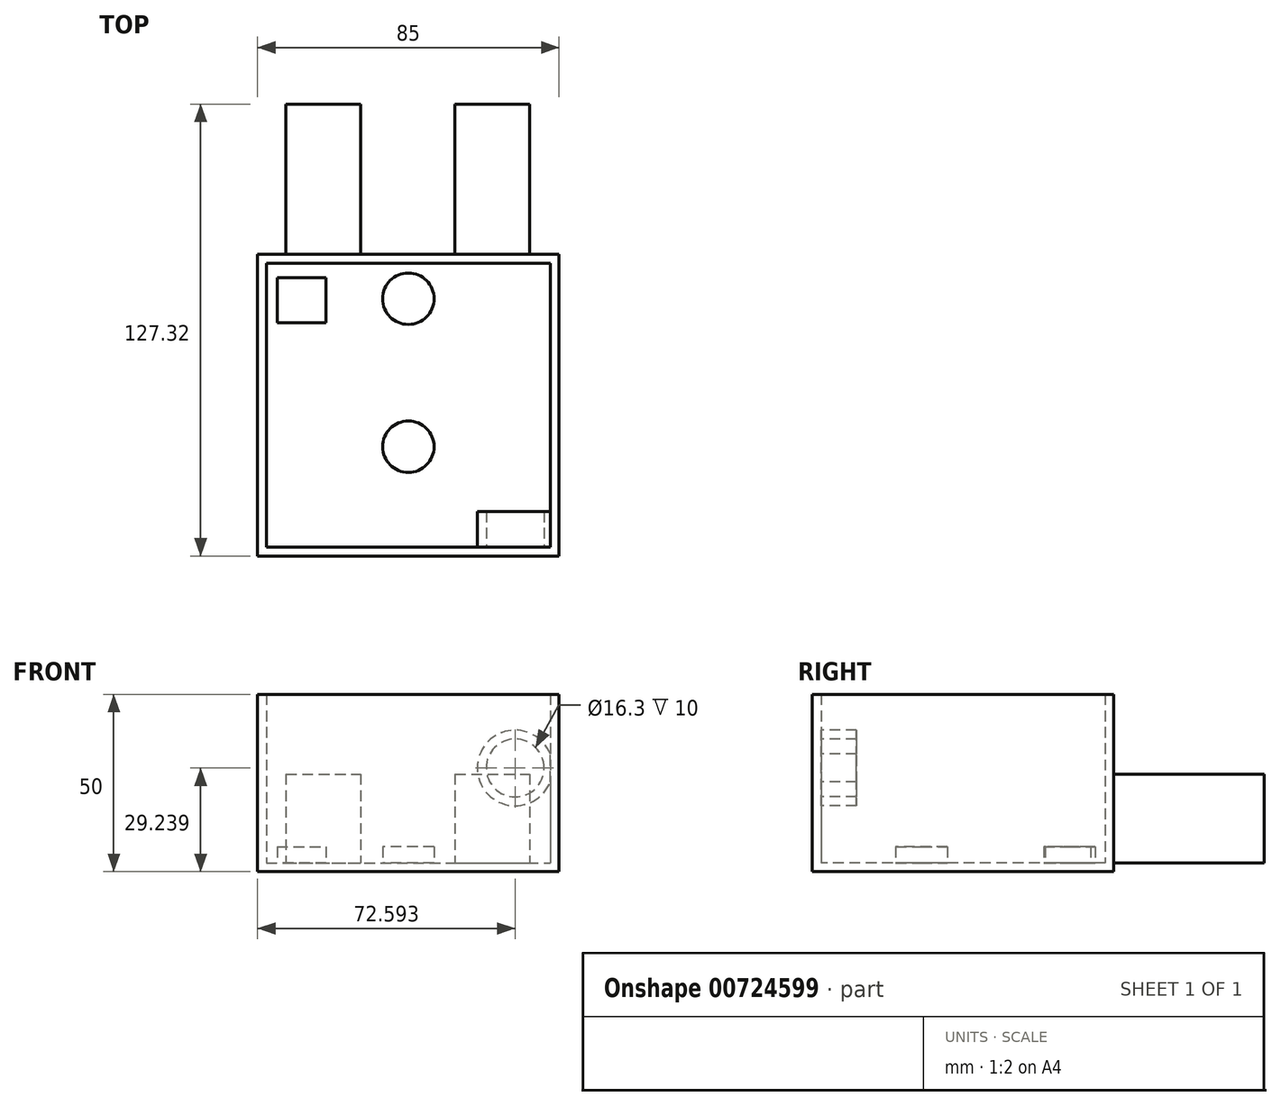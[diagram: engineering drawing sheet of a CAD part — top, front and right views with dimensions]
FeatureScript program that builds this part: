
annotation { "Feature Type Name" : "Feature", "Feature Type Description" : "" }
export const myFeature = defineFeature(function(context is Context, id is Id, definition is map)
    precondition{}
    {
        {
            var Q0;
            Q0=qCreatedBy(makeId("Top.planeOp"),FACE);
            var sketch = newSketch(context, id + "F0", { "sketchPlane" : qUnion([Q0])});
            skLineSegment(sketch, "E0.bottom", {"start": v(-42.5, 42.5) * mm, "end": v(42.5, 42.5) * mm});
            skLineSegment(sketch, "E0.top", {"start": v(-42.5, -42.5) * mm, "end": v(42.5, -42.5) * mm});
            skLineSegment(sketch, "E0.left", {"start": v(-42.5, 42.5) * mm, "end": v(-42.5, -42.5) * mm});
            skLineSegment(sketch, "E0.right", {"start": v(42.5, 42.5) * mm, "end": v(42.5, -42.5) * mm});
            skPoint(sketch, "E0.middle", {"position": v(0, 0) * mm});
            skSolve(sketch);
        }
        {
            var Q0;
            Q0=makeQuery(id+"F0.imprint","IMPRINT",FACE,{"disambiguationData":[TD([[makeQuery(id+"F0.imprint","IMPRINT",EDGE,{"derivedFrom":sQuery(id+"F0.wireOp",EDGE,"E0.bottom")}),-1.0]])]});
            extrude(context, id + "F1", {"entities" : qUnion([Q0]), "depth" : 50 * mm, "offsetDistance" : 25 * mm});
        }
        {
            var Q0;
            Q0=makeQuery(id+"F1.opExtrude","CAP_FACE",FACE,{"disambiguationData":[OSD([sQuery(id+"F0.wireOp",EDGE,"E0.bottom"),sQuery(id+"F0.wireOp",EDGE,"E0.top"),sQuery(id+"F0.wireOp",EDGE,"E0.left"),sQuery(id+"F0.wireOp",EDGE,"E0.right")])],"isStart":false});
            shell(context, id + "F2", {"entities" : qUnion([Q0]), "thickness" : 2.5 * mm});
        }
        {
            var Q0;
            Q0=makeQuery(id+"F2.opShell","OFFSET_FACE",FACE,{"disambiguationData":[OSD([sQuery(id+"F0.wireOp",EDGE,"E0.bottom"),sQuery(id+"F0.wireOp",EDGE,"E0.top"),sQuery(id+"F0.wireOp",EDGE,"E0.left"),sQuery(id+"F0.wireOp",EDGE,"E0.right")])]});
            var sketch = newSketch(context, id + "F3", { "sketchPlane" : qUnion([Q0])});
            skLineSegment(sketch, "E1.bottom", {"start": v(-13.46, 84.82) * mm, "end": v(-34.46, 84.82) * mm});
            skLineSegment(sketch, "E1.top", {"start": v(-13.46, 42.42) * mm, "end": v(-34.46, 42.42) * mm});
            skLineSegment(sketch, "E1.left", {"start": v(-13.46, 84.82) * mm, "end": v(-13.46, 42.42) * mm});
            skLineSegment(sketch, "E1.right", {"start": v(-34.46, 84.82) * mm, "end": v(-34.46, 42.42) * mm});
            skPoint(sketch, "E1.middle", {"position": v(-23.96, 63.62) * mm});
            skLineSegment(sketch, "E2.bottom", {"start": v(13.16, 84.82) * mm, "end": v(34.16, 84.82) * mm});
            skLineSegment(sketch, "E2.top", {"start": v(13.16, 42.42) * mm, "end": v(34.16, 42.42) * mm});
            skLineSegment(sketch, "E2.left", {"start": v(13.16, 84.82) * mm, "end": v(13.16, 42.42) * mm});
            skLineSegment(sketch, "E2.right", {"start": v(34.16, 84.82) * mm, "end": v(34.16, 42.42) * mm});
            skPoint(sketch, "E2.middle", {"position": v(23.66, 63.62) * mm});
            skSolve(sketch);
        }
        {
            var Q0;
            Q0=qSketchRegion(id+"F3",true);
            extrude(context, id + "F4", {"entities" : qUnion([Q0]), "operationType" : NewBodyOperationType.ADD, "depth" : 25 * mm, "offsetDistance" : 25 * mm});
        }
        {
            var Q0;
            Q0=makeQuery(id+"F2.opShell","OFFSET_FACE",FACE,{"disambiguationData":[OSD([sQuery(id+"F0.wireOp",EDGE,"E0.bottom"),sQuery(id+"F0.wireOp",EDGE,"E0.top"),sQuery(id+"F0.wireOp",EDGE,"E0.left"),sQuery(id+"F0.wireOp",EDGE,"E0.right")])]});
            var sketch = newSketch(context, id + "F5", { "sketchPlane" : qUnion([Q0])});
            skLineSegment(sketch, "E3", {"start": v(-40, -21.26) * mm, "end": v(40, -21.26) * mm});
            skLineSegment(sketch, "E4", {"start": v(-40, 0) * mm, "end": v(40, 0) * mm});
            skLineSegment(sketch, "E5", {"start": v(-40, 21.59) * mm, "end": v(40, 21.59) * mm});
            skSolve(sketch);
        }
        {
            var Q0;
            Q0=sQuery(id+"F5.wireOp",EDGE,"E5");
            var Q1;
            Q1=sQuery(id+"F5.wireOp",EDGE,"E4");
            var Q2;
            Q2=sQuery(id+"F5.wireOp",EDGE,"E3");
            extrude(context, id + "F6", {"bodyType" : ToolBodyType.SURFACE, "surfaceEntities" : qUnion([Q0, Q1, Q2]), "depth" : 30 * mm, "offsetDistance" : 25 * mm});
        }
        {
            var Q0;
            Q0=makeQuery(id+"F2.opShell","OFFSET_FACE",FACE,{"disambiguationData":[OSD([sQuery(id+"F0.wireOp",EDGE,"E0.top")])]});
            var sketch = newSketch(context, id + "F7", { "sketchPlane" : qUnion([Q0])});
            skCircle(sketch, "E6", {"center": v(-30.1, 29.24) * mm, "radius": 10.65 * mm});
            skSolve(sketch);
        }
        {
            var Q0;
            Q0=qSketchRegion(id+"F7",true);
            extrude(context, id + "F8", {"entities" : qUnion([Q0]), "operationType" : NewBodyOperationType.ADD, "depth" : 10 * mm, "offsetDistance" : 25 * mm});
        }
        {
            var Q0;
            Q0=qCreatedBy(makeId("Top.planeOp"),FACE);
            var sketch = newSketch(context, id + "F9", { "sketchPlane" : qUnion([Q0])});
            skLineSegment(sketch, "E7.bottom", {"start": v(-36.97, 36) * mm, "end": v(-23.17, 36) * mm});
            skLineSegment(sketch, "E7.top", {"start": v(-36.97, 23.2) * mm, "end": v(-23.17, 23.2) * mm});
            skLineSegment(sketch, "E7.left", {"start": v(-36.97, 36) * mm, "end": v(-36.97, 23.2) * mm});
            skLineSegment(sketch, "E7.right", {"start": v(-23.17, 36) * mm, "end": v(-23.17, 23.2) * mm});
            skPoint(sketch, "E7.middle", {"position": v(-30.07, 29.6) * mm});
            skCircle(sketch, "E8", {"center": v(0, -11.7) * mm, "radius": 7.25 * mm});
            skCircle(sketch, "E9", {"center": v(0, 30.01) * mm, "radius": 7.25 * mm});
            skSolve(sketch);
        }
        {
            var Q0;
            Q0=qSketchRegion(id+"F9",true);
            extrude(context, id + "F10", {"entities" : qUnion([Q0]), "operationType" : NewBodyOperationType.ADD, "depth" : 7 * mm, "offsetDistance" : 25 * mm});
        }
        {
            var Q0;
            Q0=makeQuery(id+"F8.opExtrude","CAP_FACE",FACE,{"disambiguationData":[OSD([sQuery(id+"F7.wireOp",EDGE,"E6")])],"isStart":false});
            shell(context, id + "F11", {"entities" : qUnion([Q0]), "thickness" : 2.5 * mm});
        }
    });
